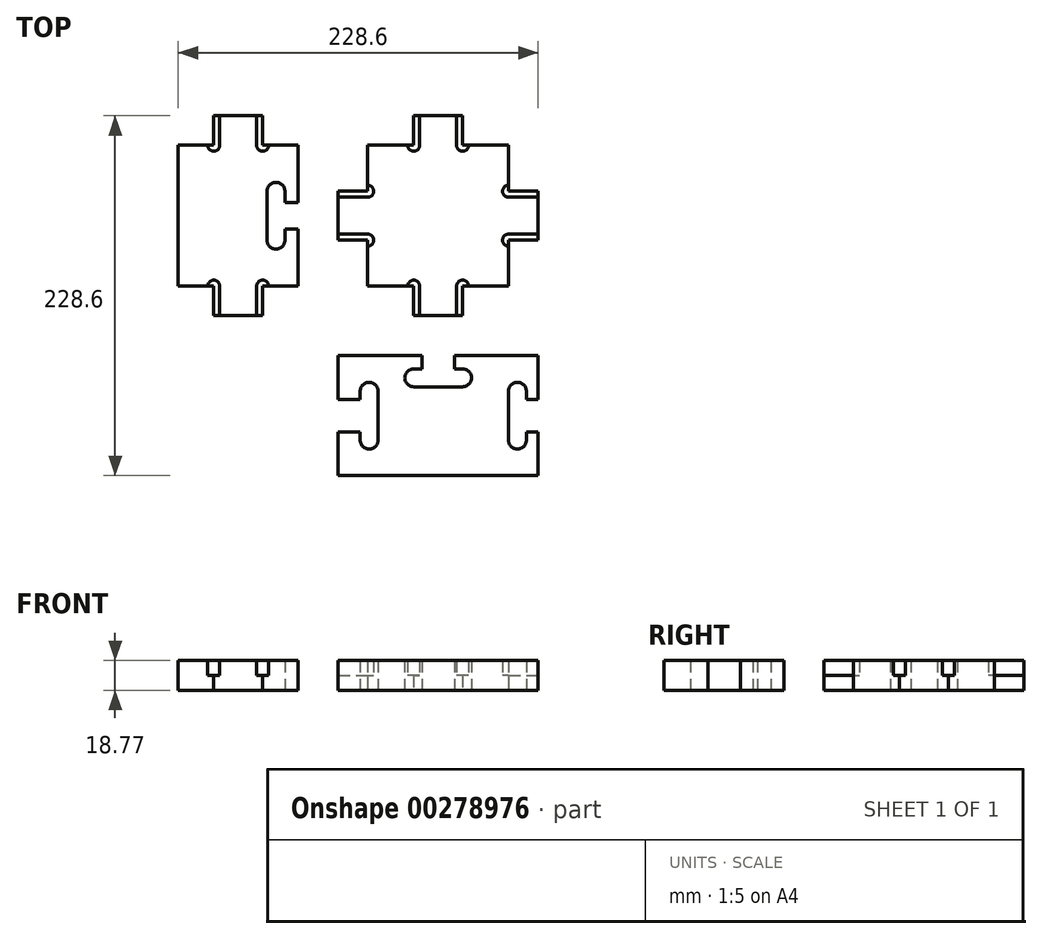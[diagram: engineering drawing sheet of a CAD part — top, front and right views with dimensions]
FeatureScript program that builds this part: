
annotation { "Feature Type Name" : "Feature", "Feature Type Description" : "" }
export const myFeature = defineFeature(function(context is Context, id is Id, definition is map)
    precondition{}
    {
        {
            assignVariable(context, id + "F0", {"name" : "THICK", "anyValue" : 18.77 * mm});
        }
        {
            var Q0;
            Q0=qCreatedBy(makeId("Top.planeOp"),FACE);
            var sketch = newSketch(context, id + "F1", { "sketchPlane" : qUnion([Q0])});
            skLineSegment(sketch, "E0.bottom", {"start": v(63.5, -63.5) * mm, "end": v(-63.5, -63.5) * mm, "construction": true});
            skLineSegment(sketch, "E0.top", {"start": v(63.5, 63.5) * mm, "end": v(-63.5, 63.5) * mm, "construction": true});
            skLineSegment(sketch, "E0.left", {"start": v(63.5, -63.5) * mm, "end": v(63.5, 63.5) * mm, "construction": true});
            skLineSegment(sketch, "E0.right", {"start": v(-63.5, -63.5) * mm, "end": v(-63.5, 63.5) * mm, "construction": true});
            skPoint(sketch, "E0.middle", {"position": v(0, 0) * mm});
            skLineSegment(sketch, "E1.bottom", {"start": v(44.73, -44.73) * mm, "end": v(15.51, -44.73) * mm});
            skLineSegment(sketch, "E1.top", {"start": v(44.73, 44.73) * mm, "end": v(15.5, 44.73) * mm});
            skLineSegment(sketch, "E1.left", {"start": v(44.73, -44.73) * mm, "end": v(44.73, -15.51) * mm});
            skLineSegment(sketch, "E1.right", {"start": v(-44.73, -44.73) * mm, "end": v(-44.73, -15.51) * mm});
            skLineSegment(sketch, "E2", {"start": v(-11.7, 63.5) * mm, "end": v(11.7, 63.5) * mm});
            skPoint(sketch, "E3", {"position": v(0, 63.5) * mm});
            skLineSegment(sketch, "E4", {"start": v(-11.7, 63.5) * mm, "end": v(-11.7, 44.73) * mm});
            skLineSegment(sketch, "E5", {"start": v(11.7, 63.5) * mm, "end": v(11.7, 44.73) * mm});
            skArc(sketch, "E6", {"start": v(-19.32, 44.73) * mm, "mid": v(-15.51, 40.92) * mm, "end": v(-11.7, 44.73) * mm});
            skLineSegment(sketch, "E7", {"start": v(-15.51, 44.73) * mm, "end": v(-15.51, 63.5) * mm});
            skLineSegment(sketch, "E8", {"start": v(-15.51, 63.5) * mm, "end": v(-11.7, 63.5) * mm});
            skArc(sketch, "E9", {"start": v(11.7, 44.73) * mm, "mid": v(15.5, 40.92) * mm, "end": v(19.32, 44.73) * mm});
            skLineSegment(sketch, "E10", {"start": v(15.5, 44.73) * mm, "end": v(15.5, 63.5) * mm});
            skLineSegment(sketch, "E11", {"start": v(15.5, 63.5) * mm, "end": v(11.7, 63.5) * mm});
            skLineSegment(sketch, "E12.trimOffspring", {"start": v(-15.51, 44.73) * mm, "end": v(-44.73, 44.73) * mm});
            skLineSegment(sketch, "E13", {"start": v(-11.7, -44.73) * mm, "end": v(-11.7, -63.5) * mm});
            skLineSegment(sketch, "E14", {"start": v(11.7, -44.73) * mm, "end": v(11.7, -63.5) * mm});
            skArc(sketch, "E15", {"start": v(-11.7, -44.73) * mm, "mid": v(-15.5, -40.92) * mm, "end": v(-19.32, -44.73) * mm});
            skArc(sketch, "E16", {"start": v(19.32, -44.73) * mm, "mid": v(15.5, -40.92) * mm, "end": v(11.7, -44.73) * mm});
            skLineSegment(sketch, "E17", {"start": v(-15.51, -44.73) * mm, "end": v(-15.51, -63.5) * mm});
            skLineSegment(sketch, "E18", {"start": v(-15.5, -63.5) * mm, "end": v(-11.7, -63.5) * mm});
            skLineSegment(sketch, "E19", {"start": v(15.51, -44.73) * mm, "end": v(15.51, -63.5) * mm});
            skLineSegment(sketch, "E20", {"start": v(15.51, -63.5) * mm, "end": v(11.7, -63.5) * mm});
            skLineSegment(sketch, "E21", {"start": v(11.7, -63.5) * mm, "end": v(-11.7, -63.5) * mm});
            skLineSegment(sketch, "E22.trimOffspring", {"start": v(-15.51, -44.73) * mm, "end": v(-44.73, -44.73) * mm});
            skLineSegment(sketch, "E23", {"start": v(-63.5, 11.7) * mm, "end": v(-63.5, -11.7) * mm});
            skPoint(sketch, "E24", {"position": v(-63.5, 0) * mm});
            skLineSegment(sketch, "E25", {"start": v(-63.5, 11.7) * mm, "end": v(-44.73, 11.7) * mm});
            skLineSegment(sketch, "E26", {"start": v(-63.5, -11.7) * mm, "end": v(-44.73, -11.7) * mm});
            skArc(sketch, "E27", {"start": v(-44.73, 11.7) * mm, "mid": v(-40.92, 15.51) * mm, "end": v(-44.73, 19.32) * mm});
            skArc(sketch, "E28", {"start": v(-44.73, -19.32) * mm, "mid": v(-40.92, -15.51) * mm, "end": v(-44.73, -11.7) * mm});
            skLineSegment(sketch, "E29", {"start": v(-44.73, 15.51) * mm, "end": v(-63.5, 15.5) * mm});
            skLineSegment(sketch, "E30", {"start": v(-63.5, 15.5) * mm, "end": v(-63.5, 11.7) * mm});
            skLineSegment(sketch, "E31", {"start": v(-44.73, -15.51) * mm, "end": v(-63.5, -15.51) * mm});
            skLineSegment(sketch, "E32", {"start": v(-63.5, -15.51) * mm, "end": v(-63.5, -11.7) * mm});
            skLineSegment(sketch, "E33.trimOffspring", {"start": v(-44.73, 15.51) * mm, "end": v(-44.73, 44.73) * mm});
            skLineSegment(sketch, "E34", {"start": v(44.73, 11.7) * mm, "end": v(63.5, 11.7) * mm});
            skLineSegment(sketch, "E35", {"start": v(44.73, -11.7) * mm, "end": v(63.5, -11.7) * mm});
            skLineSegment(sketch, "E36", {"start": v(63.5, 11.7) * mm, "end": v(63.5, -11.7) * mm});
            skArc(sketch, "E37", {"start": v(44.73, 19.32) * mm, "mid": v(40.92, 15.51) * mm, "end": v(44.73, 11.7) * mm});
            skArc(sketch, "E38", {"start": v(44.73, -11.7) * mm, "mid": v(40.92, -15.51) * mm, "end": v(44.73, -19.32) * mm});
            skLineSegment(sketch, "E39", {"start": v(44.73, 15.51) * mm, "end": v(63.5, 15.51) * mm});
            skLineSegment(sketch, "E40", {"start": v(63.5, 15.51) * mm, "end": v(63.5, 11.7) * mm});
            skLineSegment(sketch, "E41", {"start": v(44.73, -15.51) * mm, "end": v(63.5, -15.51) * mm});
            skLineSegment(sketch, "E42", {"start": v(63.5, -15.51) * mm, "end": v(63.5, -11.7) * mm});
            skLineSegment(sketch, "E43.trimOffspring", {"start": v(44.73, 15.51) * mm, "end": v(44.73, 44.73) * mm});
            skLineSegment(sketch, "E44", {"start": v(0, 0) * mm, "end": v(-127, 0) * mm, "construction": true});
            skLineSegment(sketch, "E45.right", {"start": v(-165.1, -63.5) * mm, "end": v(-165.1, 63.5) * mm, "construction": true});
            skPoint(sketch, "E45.middle", {"position": v(-127, 0) * mm});
            skLineSegment(sketch, "E46.bottom", {"start": v(-88.9, -44.73) * mm, "end": v(-111.5, -44.73) * mm});
            skLineSegment(sketch, "E46.top", {"start": v(-88.9, 44.73) * mm, "end": v(-111.5, 44.73) * mm});
            skLineSegment(sketch, "E46.left", {"start": v(-88.9, -44.73) * mm, "end": v(-88.9, -8.39) * mm});
            skLineSegment(sketch, "E46.right", {"start": v(-165.1, -44.73) * mm, "end": v(-165.1, 44.73) * mm});
            skLineSegment(sketch, "E47", {"start": v(-108.67, 15.5) * mm, "end": v(-108.67, -15.51) * mm});
            skLineSegment(sketch, "E48", {"start": v(-108.67, 15.5) * mm, "end": v(-97.29, 15.5) * mm, "construction": true});
            skLineSegment(sketch, "E49", {"start": v(-97.29, 15.5) * mm, "end": v(-97.29, 8.39) * mm});
            skLineSegment(sketch, "E50", {"start": v(-97.29, -15.51) * mm, "end": v(-108.67, -15.51) * mm, "construction": true});
            skLineSegment(sketch, "E51.trimOffspring", {"start": v(-97.29, -8.39) * mm, "end": v(-97.29, -15.51) * mm});
            skArc(sketch, "E52", {"start": v(-108.67, 15.5) * mm, "mid": v(-102.98, 21.2) * mm, "end": v(-97.29, 15.5) * mm});
            skArc(sketch, "E53", {"start": v(-97.29, -15.51) * mm, "mid": v(-102.98, -21.2) * mm, "end": v(-108.67, -15.51) * mm});
            skLineSegment(sketch, "E54", {"start": v(-88.9, 8.39) * mm, "end": v(-88.9, 44.73) * mm});
            skLineSegment(sketch, "E55", {"start": v(-138.7, 63.5) * mm, "end": v(-115.3, 63.5) * mm});
            skPoint(sketch, "E56", {"position": v(-127, 63.5) * mm});
            skLineSegment(sketch, "E57", {"start": v(-115.3, 63.5) * mm, "end": v(-115.3, 44.73) * mm});
            skLineSegment(sketch, "E58", {"start": v(-138.7, 63.5) * mm, "end": v(-138.7, 44.73) * mm});
            skArc(sketch, "E59", {"start": v(-115.3, 44.73) * mm, "mid": v(-111.5, 40.92) * mm, "end": v(-107.68, 44.73) * mm});
            skArc(sketch, "E60", {"start": v(-146.32, 44.73) * mm, "mid": v(-142.51, 40.92) * mm, "end": v(-138.7, 44.73) * mm});
            skLineSegment(sketch, "E61", {"start": v(-138.7, -63.5) * mm, "end": v(-115.3, -63.5) * mm});
            skPoint(sketch, "E62", {"position": v(-127, -63.5) * mm});
            skLineSegment(sketch, "E63", {"start": v(-142.51, 44.73) * mm, "end": v(-142.51, 63.5) * mm});
            skLineSegment(sketch, "E64", {"start": v(-142.51, 63.5) * mm, "end": v(-138.7, 63.5) * mm});
            skLineSegment(sketch, "E65", {"start": v(-111.5, 44.73) * mm, "end": v(-111.5, 63.5) * mm});
            skLineSegment(sketch, "E66", {"start": v(-111.5, 63.5) * mm, "end": v(-115.3, 63.5) * mm});
            skLineSegment(sketch, "E67.trimOffspring", {"start": v(-142.51, 44.73) * mm, "end": v(-165.1, 44.73) * mm});
            skLineSegment(sketch, "E68", {"start": v(-115.3, -63.5) * mm, "end": v(-115.3, -44.73) * mm});
            skLineSegment(sketch, "E69", {"start": v(-138.7, -63.5) * mm, "end": v(-138.7, -44.73) * mm});
            skLineSegment(sketch, "E70", {"start": v(-111.5, -44.73) * mm, "end": v(-111.5, -63.5) * mm});
            skLineSegment(sketch, "E71", {"start": v(-111.5, -63.5) * mm, "end": v(-115.3, -63.5) * mm});
            skLineSegment(sketch, "E72", {"start": v(-142.51, -44.73) * mm, "end": v(-142.51, -63.5) * mm});
            skLineSegment(sketch, "E73", {"start": v(-142.51, -63.5) * mm, "end": v(-138.7, -63.5) * mm});
            skArc(sketch, "E74", {"start": v(-146.32, -44.73) * mm, "mid": v(-142.51, -40.92) * mm, "end": v(-138.7, -44.73) * mm});
            skLineSegment(sketch, "E75.trimOffspring", {"start": v(-142.51, -44.73) * mm, "end": v(-165.1, -44.73) * mm});
            skArc(sketch, "E76", {"start": v(-107.68, -44.73) * mm, "mid": v(-111.5, -40.92) * mm, "end": v(-115.3, -44.73) * mm});
            skLineSegment(sketch, "E77", {"start": v(0, 0) * mm, "end": v(0, -127) * mm, "construction": true});
            skLineSegment(sketch, "E78.top", {"start": v(-63.5, -165.1) * mm, "end": v(63.5, -165.1) * mm});
            skLineSegment(sketch, "E78.left", {"start": v(-63.5, -88.9) * mm, "end": v(-63.5, -116.61) * mm});
            skLineSegment(sketch, "E78.right", {"start": v(63.5, -88.9) * mm, "end": v(63.5, -116.61) * mm});
            skPoint(sketch, "E78.middle", {"position": v(0, -127) * mm});
            skLineSegment(sketch, "E79", {"start": v(-165.1, -88.9) * mm, "end": v(-88.9, -88.9) * mm, "construction": true});
            skLineSegment(sketch, "E80", {"start": v(-15.5, -97.29) * mm, "end": v(-15.5, -108.67) * mm, "construction": true});
            skLineSegment(sketch, "E81", {"start": v(15.51, -97.29) * mm, "end": v(15.51, -108.67) * mm, "construction": true});
            skLineSegment(sketch, "E82", {"start": v(-15.5, -97.29) * mm, "end": v(-10.39, -97.29) * mm});
            skLineSegment(sketch, "E83", {"start": v(10.39, -97.29) * mm, "end": v(15.5, -97.29) * mm});
            skLineSegment(sketch, "E84", {"start": v(15.5, -108.67) * mm, "end": v(-15.5, -108.67) * mm});
            skArc(sketch, "E85", {"start": v(-15.5, -97.29) * mm, "mid": v(-21.2, -102.98) * mm, "end": v(-15.5, -108.67) * mm});
            skArc(sketch, "E86", {"start": v(15.5, -108.67) * mm, "mid": v(21.2, -102.98) * mm, "end": v(15.5, -97.29) * mm});
            skLineSegment(sketch, "E87", {"start": v(-63.5, -127) * mm, "end": v(63.5, -127) * mm, "construction": true});
            skLineSegment(sketch, "E88", {"start": v(-38.1, -111.49) * mm, "end": v(-38.1, -142.51) * mm});
            skPoint(sketch, "E89", {"position": v(-38.1, -127) * mm});
            skLineSegment(sketch, "E90", {"start": v(-38.1, -111.49) * mm, "end": v(-49.48, -111.49) * mm, "construction": true});
            skLineSegment(sketch, "E91", {"start": v(-49.48, -111.5) * mm, "end": v(-49.48, -116.61) * mm});
            skLineSegment(sketch, "E92", {"start": v(-49.48, -137.39) * mm, "end": v(-49.48, -142.5) * mm});
            skLineSegment(sketch, "E93", {"start": v(-49.48, -142.51) * mm, "end": v(-38.1, -142.51) * mm, "construction": true});
            skLineSegment(sketch, "E94", {"start": v(-49.48, -116.61) * mm, "end": v(-49.48, -137.39) * mm, "construction": true});
            skPoint(sketch, "E95", {"position": v(-49.48, -127) * mm});
            skArc(sketch, "E96", {"start": v(-38.1, -111.49) * mm, "mid": v(-43.79, -105.8) * mm, "end": v(-49.48, -111.5) * mm});
            skArc(sketch, "E97", {"start": v(-38.1, -142.51) * mm, "mid": v(-43.79, -148.2) * mm, "end": v(-49.48, -142.5) * mm});
            skLineSegment(sketch, "E98.trimOffspring", {"start": v(-63.5, -137.39) * mm, "end": v(-63.5, -165.1) * mm});
            skLineSegment(sketch, "E99", {"start": v(-88.9, -88.9) * mm, "end": v(-88.9, -165.1) * mm, "construction": true});
            skLineSegment(sketch, "E100", {"start": v(56.05, -116.61) * mm, "end": v(56.05, -111.49) * mm});
            skLineSegment(sketch, "E101", {"start": v(56.05, -111.49) * mm, "end": v(44.67, -111.49) * mm, "construction": true});
            skLineSegment(sketch, "E102", {"start": v(44.67, -111.49) * mm, "end": v(44.67, -142.51) * mm});
            skLineSegment(sketch, "E103", {"start": v(44.67, -142.51) * mm, "end": v(56.05, -142.51) * mm, "construction": true});
            skLineSegment(sketch, "E104", {"start": v(56.05, -142.51) * mm, "end": v(56.05, -137.39) * mm});
            skArc(sketch, "E105", {"start": v(44.67, -111.49) * mm, "mid": v(50.36, -105.8) * mm, "end": v(56.05, -111.49) * mm});
            skArc(sketch, "E106", {"start": v(56.05, -142.51) * mm, "mid": v(50.36, -148.2) * mm, "end": v(44.67, -142.51) * mm});
            skLineSegment(sketch, "E107.trimOffspring", {"start": v(63.5, -137.39) * mm, "end": v(63.5, -165.1) * mm});
            skPoint(sketch, "E108", {"position": v(-127, -88.9) * mm});
            skLineSegment(sketch, "E109", {"start": v(-88.9, 8.39) * mm, "end": v(-97.29, 8.39) * mm});
            skLineSegment(sketch, "E110", {"start": v(-88.9, -8.39) * mm, "end": v(-97.29, -8.39) * mm});
            skLineSegment(sketch, "E111", {"start": v(-88.9, 8.39) * mm, "end": v(-88.9, -8.39) * mm, "construction": true});
            skPoint(sketch, "E112", {"position": v(-88.9, 0) * mm});
            skLineSegment(sketch, "E113", {"start": v(-63.5, -88.9) * mm, "end": v(-10.39, -88.9) * mm});
            skLineSegment(sketch, "E114", {"start": v(-49.48, -137.39) * mm, "end": v(-63.5, -137.39) * mm});
            skLineSegment(sketch, "E115", {"start": v(-49.48, -116.61) * mm, "end": v(-63.5, -116.61) * mm});
            skLineSegment(sketch, "E116", {"start": v(63.5, -88.9) * mm, "end": v(10.39, -88.9) * mm});
            skLineSegment(sketch, "E117", {"start": v(10.39, -88.9) * mm, "end": v(10.39, -97.29) * mm});
            skLineSegment(sketch, "E118", {"start": v(-10.39, -88.9) * mm, "end": v(-10.39, -97.29) * mm});
            skLineSegment(sketch, "E119", {"start": v(56.05, -116.61) * mm, "end": v(63.5, -116.61) * mm});
            skLineSegment(sketch, "E120", {"start": v(56.05, -137.39) * mm, "end": v(63.5, -137.39) * mm});
            skSolve(sketch);
        }
        {
            var Q0;
            Q0=makeQuery(id+"F1.imprint","IMPRINT",FACE,{"disambiguationData":[TD([[makeQuery(id+"F1.imprint","IMPRINT",EDGE,{"derivedFrom":sQuery(id+"F1.wireOp",EDGE,"E2")}),-1.0]])]});
            extrude(context, id + "F2", {"entities" : qUnion([Q0]), "depth" : getVariable(context, 'THICK')});
        }
        {
            var Q0;
            Q0=makeQuery(id+"F1.imprint","IMPRINT",FACE,{"disambiguationData":[TD([[makeQuery(id+"F1.imprint","IMPRINT",EDGE,{"derivedFrom":sQuery(id+"F1.wireOp",EDGE,"E4")}),-1.0]])]});
            var Q1;
            Q1=makeQuery(id+"F1.imprint","IMPRINT",FACE,{"disambiguationData":[TD([[makeQuery(id+"F1.imprint","IMPRINT",EDGE,{"derivedFrom":sQuery(id+"F1.wireOp",EDGE,"E25")}),1.0]])]});
            var Q2;
            Q2=makeQuery(id+"F1.imprint","IMPRINT",FACE,{"disambiguationData":[TD([[makeQuery(id+"F1.imprint","IMPRINT",EDGE,{"derivedFrom":sQuery(id+"F1.wireOp",EDGE,"E26")}),-1.0]])]});
            var Q3;
            Q3=makeQuery(id+"F1.imprint","IMPRINT",FACE,{"disambiguationData":[TD([[makeQuery(id+"F1.imprint","IMPRINT",EDGE,{"derivedFrom":sQuery(id+"F1.wireOp",EDGE,"E13")}),-1.0]])]});
            var Q4;
            Q4=makeQuery(id+"F1.imprint","IMPRINT",FACE,{"disambiguationData":[TD([[makeQuery(id+"F1.imprint","IMPRINT",EDGE,{"derivedFrom":sQuery(id+"F1.wireOp",EDGE,"E14")}),1.0]])]});
            var Q5;
            Q5=makeQuery(id+"F1.imprint","IMPRINT",FACE,{"disambiguationData":[TD([[makeQuery(id+"F1.imprint","IMPRINT",EDGE,{"derivedFrom":sQuery(id+"F1.wireOp",EDGE,"E35")}),-1.0]])]});
            var Q6;
            Q6=makeQuery(id+"F1.imprint","IMPRINT",FACE,{"disambiguationData":[TD([[makeQuery(id+"F1.imprint","IMPRINT",EDGE,{"derivedFrom":sQuery(id+"F1.wireOp",EDGE,"E34")}),1.0]])]});
            var Q7;
            Q7=makeQuery(id+"F1.imprint","IMPRINT",FACE,{"disambiguationData":[TD([[makeQuery(id+"F1.imprint","IMPRINT",EDGE,{"derivedFrom":sQuery(id+"F1.wireOp",EDGE,"E5")}),1.0]])]});
            extrude(context, id + "F3", {"entities" : qUnion([Q0, Q1, Q2, Q3, Q4, Q5, Q6, Q7]), "operationType" : NewBodyOperationType.ADD, "depth" : getVariable(context, 'THICK') / 2});
        }
        {
            var Q0;
            Q0=makeQuery(id+"F1.imprint","IMPRINT",FACE,{"disambiguationData":[TD([[makeQuery(id+"F1.imprint","IMPRINT",EDGE,{"derivedFrom":sQuery(id+"F1.wireOp",EDGE,"E78.top")}),1.0]])]});
            extrude(context, id + "F4", {"entities" : qUnion([Q0]), "depth" : getVariable(context, 'THICK')});
        }
        {
            var Q0;
            {var subQ6=sQuery(id+"F1.wireOp",EDGE,"E46.left");Q0=makeQuery(id+"F1.imprint","IMPRINT",FACE,{"disambiguationData":[TD([[makeQuery(id+"F1.imprint","IMPRINT",EDGE,{"derivedFrom":subQ6}),1.0]])]});}
            extrude(context, id + "F5", {"entities" : qUnion([Q0]), "depth" : getVariable(context, 'THICK')});
        }
        {
            var Q0;
            Q0=makeQuery(id+"F1.imprint","IMPRINT",FACE,{"disambiguationData":[TD([[makeQuery(id+"F1.imprint","IMPRINT",EDGE,{"derivedFrom":sQuery(id+"F1.wireOp",EDGE,"E58")}),-1.0]])]});
            var Q1;
            Q1=makeQuery(id+"F1.imprint","IMPRINT",FACE,{"disambiguationData":[TD([[makeQuery(id+"F1.imprint","IMPRINT",EDGE,{"derivedFrom":sQuery(id+"F1.wireOp",EDGE,"E57")}),1.0]])]});
            var Q2;
            Q2=makeQuery(id+"F1.imprint","IMPRINT",FACE,{"disambiguationData":[TD([[makeQuery(id+"F1.imprint","IMPRINT",EDGE,{"derivedFrom":sQuery(id+"F1.wireOp",EDGE,"E68")}),-1.0]])]});
            var Q3;
            Q3=makeQuery(id+"F1.imprint","IMPRINT",FACE,{"disambiguationData":[TD([[makeQuery(id+"F1.imprint","IMPRINT",EDGE,{"derivedFrom":sQuery(id+"F1.wireOp",EDGE,"E69")}),1.0]])]});
            extrude(context, id + "F6", {"entities" : qUnion([Q0, Q1, Q2, Q3]), "operationType" : NewBodyOperationType.ADD, "depth" : getVariable(context, 'THICK') / 2});
        }
    });
